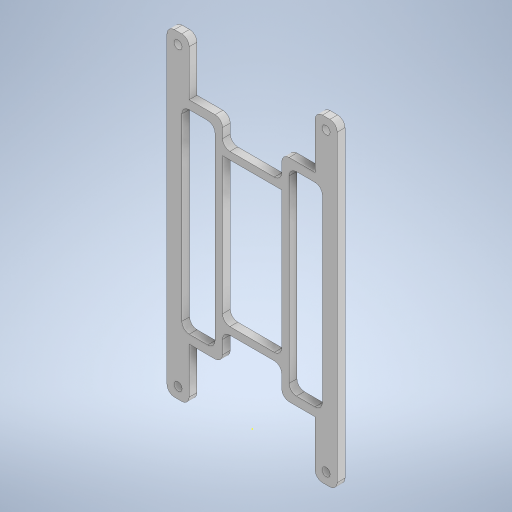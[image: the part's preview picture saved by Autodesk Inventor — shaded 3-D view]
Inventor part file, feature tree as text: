
AUTODESK INVENTOR PART (.ipt)
format: ipt  version: 2024 (Build 280153000, 153)  size: 438,784 bytes
history: native  units: in
note: dims shown in document units (in); Inventor stores cm internally (conversion verified against a paired STEP export)
features: sketch x7, extrude x7, fillet x2, other x1
ambient origin geometry x8: Origin, YZ Plane, XZ Plane, XY Plane, X Axis, Y Axis, Z Axis, Center Point
bodies: Solid1 (feature_tree)
feature tree (17):
  sketch  "Sketch1"  dims[d5=0.1181in d6=0.0in d7=0.1181in d8=0.0in]
  extrude  "Extrusion1"  Depth=0.1181in TaperAngle=0.0deg
  extrude  "Extrusion2"  Depth=0.0787in TaperAngle=0.0deg
  extrude  "Extrusion3"  Depth=0.0787in TaperAngle=0.0deg
  extrude  "Wyciągnięcie proste4"  Depth=0.0787in TaperAngle=0.0deg
  extrude  "Wyciągnięcie proste5"  Depth=0.0787in TaperAngle=0.0deg
  extrude  "Wyciągnięcie proste6"  Depth=0.0787in
  fillet  "Zaokrąglenie1"  Radius=0.3937in
  sketch  "Szkic7"
  extrude  "Wyciągnięcie proste8"  Depth=0.0787in
  fillet  "Zaokrąglenie2"  Radius=0.0039in
  other  "Pogrubienie1"
  sketch  "Sketch2"  dims[d9=0.0787in d10=0.0394in d11=0.0in d12=0.0787in d13=0.0in d14=0.0787in d15=0.0in d16=0.0787in d17=0.0in d18=0.0787in d21=0.3937in d22=0.0in d23=0.0787in d24=0.0039in d25=0.0039in]
  sketch  "Szkic3"
  sketch  "Szkic4"
  sketch  "Szkic5"
  sketch  "Szkic8"
